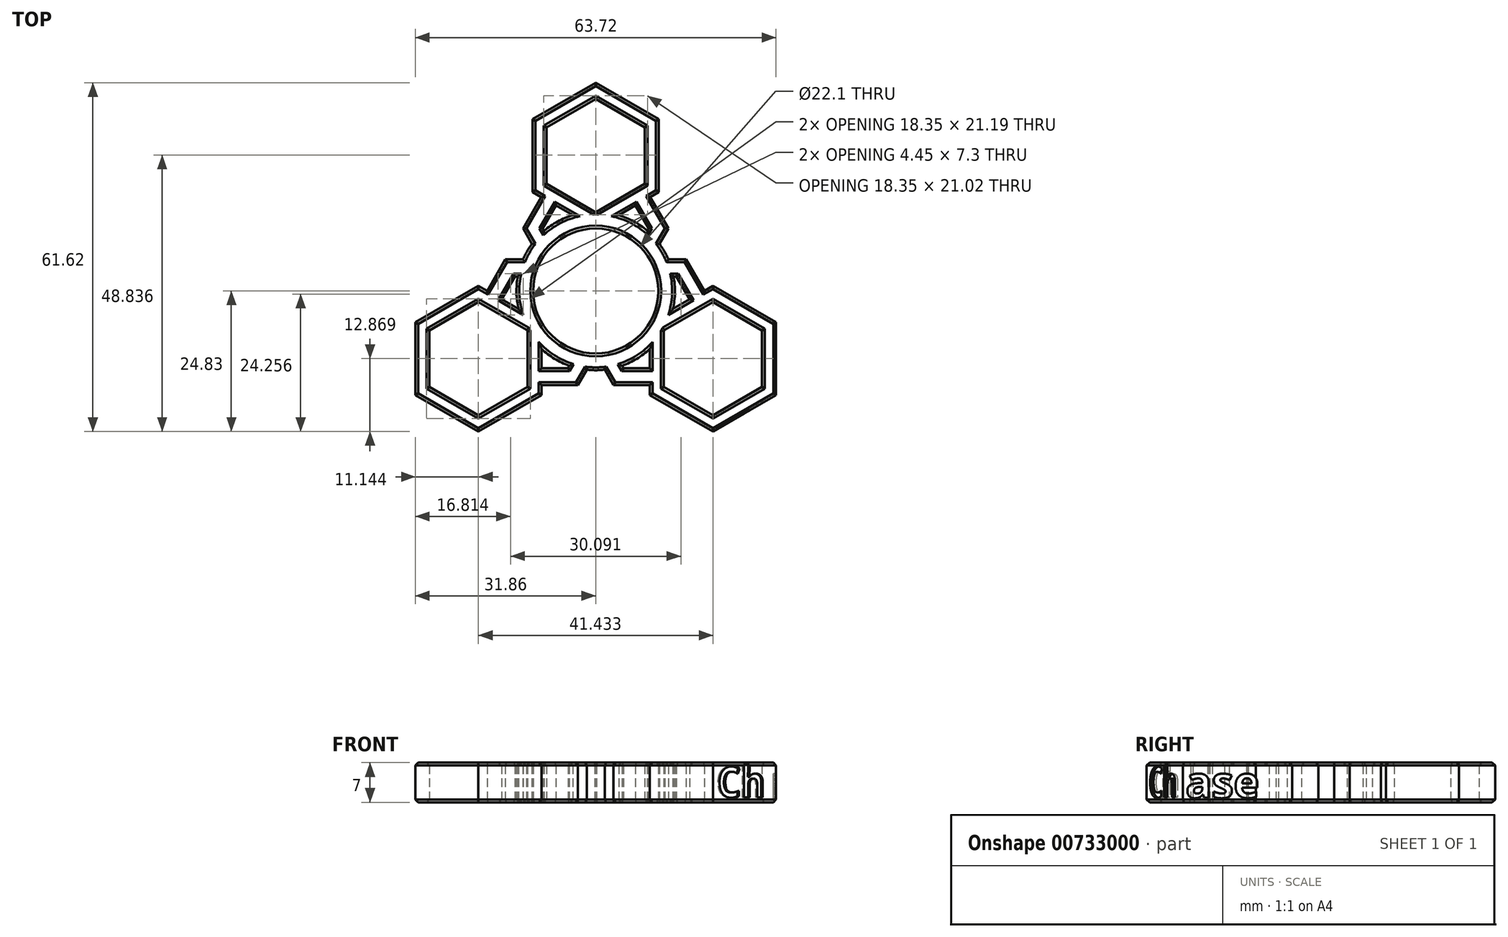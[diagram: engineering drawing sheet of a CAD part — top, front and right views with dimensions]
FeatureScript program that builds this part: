
annotation { "Feature Type Name" : "Feature", "Feature Type Description" : "" }
export const myFeature = defineFeature(function(context is Context, id is Id, definition is map)
    precondition{}
    {
        {
            var Q0;
            Q0=qCreatedBy(makeId("Top.planeOp"),FACE);
            var sketch = newSketch(context, id + "F0", { "sketchPlane" : qUnion([Q0])});
            skCircle(sketch, "E0", {"center": v(0, 0) * mm, "radius": 11.05 * mm});
            skCircle(sketch, "E1.cCircle", {"center": v(0, 23.92) * mm, "radius": 10.02 * mm, "construction": true});
            skLineSegment(sketch, "E1.0", {"start": v(0, 33.94) * mm, "end": v(8.68, 28.93) * mm});
            skLineSegment(sketch, "E1.1", {"start": v(8.67, 28.93) * mm, "end": v(8.68, 18.91) * mm});
            skLineSegment(sketch, "E1.2", {"start": v(8.67, 18.91) * mm, "end": v(0, 13.9) * mm});
            skLineSegment(sketch, "E1.3", {"start": v(0, 13.9) * mm, "end": v(-8.67, 18.91) * mm});
            skLineSegment(sketch, "E1.4", {"start": v(-8.67, 18.91) * mm, "end": v(-8.68, 28.93) * mm});
            skLineSegment(sketch, "E1.5", {"start": v(-8.67, 28.93) * mm, "end": v(0, 33.94) * mm});
            skCircle(sketch, "E2.cCircle", {"center": v(0, 11.05) * mm, "radius": 9.36 * mm, "construction": true});
            skLineSegment(sketch, "E2.0", {"start": v(9.36, 11.05) * mm, "end": v(4.68, 2.95) * mm});
            skLineSegment(sketch, "E2.1", {"start": v(4.68, 2.95) * mm, "end": v(-4.68, 2.95) * mm});
            skLineSegment(sketch, "E2.2", {"start": v(-4.68, 2.95) * mm, "end": v(-9.36, 11.05) * mm});
            skLineSegment(sketch, "E2.3", {"start": v(-9.36, 11.05) * mm, "end": v(-4.68, 19.15) * mm});
            skLineSegment(sketch, "E2.4", {"start": v(-4.68, 19.15) * mm, "end": v(4.68, 19.15) * mm});
            skLineSegment(sketch, "E2.5", {"start": v(4.68, 19.15) * mm, "end": v(9.36, 11.05) * mm});
            skLineSegment(sketch, "E3", {"start": v(0, 11.05) * mm, "end": v(30.07, 11.05) * mm, "construction": true});
            skLineSegment(sketch, "E4.0", {"start": v(-6.4, -0.05) * mm, "end": v(-12.82, 11.05) * mm});
            skLineSegment(sketch, "E4.1", {"start": v(-6.4, 22.15) * mm, "end": v(6.4, 22.15) * mm});
            skLineSegment(sketch, "E4.2", {"start": v(6.4, 22.15) * mm, "end": v(12.82, 11.05) * mm});
            skLineSegment(sketch, "E4.3", {"start": v(-12.82, 11.05) * mm, "end": v(-6.4, 22.15) * mm});
            skLineSegment(sketch, "E4.4", {"start": v(12.82, 11.05) * mm, "end": v(6.4, -0.05) * mm});
            skLineSegment(sketch, "E4.5", {"start": v(6.4, -0.05) * mm, "end": v(-6.4, -0.05) * mm});
            skCircle(sketch, "E5", {"center": v(0, 0) * mm, "radius": 14 * mm});
            skCircle(sketch, "E6.cCircle", {"center": v(0, 23.92) * mm, "radius": 12.87 * mm, "construction": true});
            skLineSegment(sketch, "E6.0", {"start": v(0, 11.05) * mm, "end": v(-11.15, 17.49) * mm});
            skLineSegment(sketch, "E6.1", {"start": v(-11.15, 17.49) * mm, "end": v(-11.15, 30.36) * mm});
            skLineSegment(sketch, "E6.2", {"start": v(-11.15, 30.36) * mm, "end": v(0, 36.8) * mm});
            skLineSegment(sketch, "E6.3", {"start": v(0, 36.8) * mm, "end": v(11.15, 30.36) * mm});
            skLineSegment(sketch, "E6.4", {"start": v(11.15, 30.36) * mm, "end": v(11.15, 17.49) * mm});
            skLineSegment(sketch, "E6.5", {"start": v(11.15, 17.49) * mm, "end": v(0, 11.05) * mm});
            skSolve(sketch);
        }
        {
            var Q0;
            {var subQ5=sQuery(id+"F0.wireOp",EDGE,"E1.0");Q0=makeQuery(id+"F0.imprint","IMPRINT",FACE,{"disambiguationData":[TD([[makeQuery(id+"F0.imprint","IMPRINT",EDGE,{"derivedFrom":subQ5}),1.0]])]});}
            var Q1;
            {var subQ1=sQuery(id+"F0.wireOp",EDGE,"E1.3");var subQ5=sQuery(id+"F0.wireOp",EDGE,"E1.4");var subQ6=makeQuery(id+"F0.imprint","INTERSECT",VERTEX,{"derivedFrom":[subQ1,subQ5]});Q1=makeQuery(id+"F0.imprint","IMPRINT",FACE,{"disambiguationData":[TD([[makeQuery(id+"F0.imprint","IMPRINT",EDGE,{"disambiguationData":[TD([[subQ6,1.0]])],"derivedFrom":subQ1}),1.0]])]});}
            var Q2;
            {var subQ1=sQuery(id+"F0.wireOp",EDGE,"E1.2");var subQ6=sQuery(id+"F0.wireOp",EDGE,"E1.3");var subQ13=makeQuery(id+"F0.imprint","INTERSECT",VERTEX,{"derivedFrom":[subQ1,subQ6]});Q2=makeQuery(id+"F0.imprint","IMPRINT",FACE,{"disambiguationData":[TD([[makeQuery(id+"F0.imprint","IMPRINT",EDGE,{"disambiguationData":[TD([[subQ13,1.0]])],"derivedFrom":subQ1}),1.0]])]});}
            var Q3;
            {var subQ3=sQuery(id+"F0.wireOp",EDGE,"E1.1");var subQ5=sQuery(id+"F0.wireOp",EDGE,"E1.2");var subQ6=makeQuery(id+"F0.imprint","INTERSECT",VERTEX,{"derivedFrom":[subQ3,subQ5]});Q3=makeQuery(id+"F0.imprint","IMPRINT",FACE,{"disambiguationData":[TD([[makeQuery(id+"F0.imprint","IMPRINT",EDGE,{"disambiguationData":[TD([[subQ6,1.0]])],"derivedFrom":subQ3}),1.0]])]});}
            var Q4;
            {var subQ5=sQuery(id+"F0.wireOp",EDGE,"E2.5");var subQ6=sQuery(id+"F0.wireOp",EDGE,"E2.0");var subQ7=makeQuery(id+"F0.imprint","INTERSECT",VERTEX,{"derivedFrom":[subQ6,subQ5]});Q4=makeQuery(id+"F0.imprint","IMPRINT",FACE,{"disambiguationData":[TD([[makeQuery(id+"F0.imprint","IMPRINT",EDGE,{"disambiguationData":[TD([[subQ7,-1.0]])],"derivedFrom":subQ6}),1.0]])]});}
            var Q5;
            {var subQ0=sQuery(id+"F0.wireOp",EDGE,"E2.0");var subQ1=sQuery(id+"F0.wireOp",EDGE,"E0");var subQ2=makeQuery(id+"F0.imprint","INTERSECT",VERTEX,{"derivedFrom":[subQ1,subQ0]});Q5=makeQuery(id+"F0.imprint","IMPRINT",FACE,{"disambiguationData":[TD([[makeQuery(id+"F0.imprint","IMPRINT",EDGE,{"disambiguationData":[TD([[subQ2,1.0]])],"derivedFrom":subQ1}),-1.0]])]});}
            var Q6;
            {var subQ1=sQuery(id+"F0.wireOp",EDGE,"E0");var subQ3=sQuery(id+"F0.wireOp",EDGE,"E2.0");var subQ4=makeQuery(id+"F0.imprint","INTERSECT",VERTEX,{"derivedFrom":[subQ1,subQ3]});Q6=makeQuery(id+"F0.imprint","IMPRINT",FACE,{"disambiguationData":[TD([[makeQuery(id+"F0.imprint","IMPRINT",EDGE,{"disambiguationData":[TD([[subQ4,1.0]])],"derivedFrom":subQ3}),-1.0]])]});}
            var Q7;
            {var subQ1=sQuery(id+"F0.wireOp",EDGE,"E0");var subQ3=sQuery(id+"F0.wireOp",EDGE,"E2.2");var subQ4=makeQuery(id+"F0.imprint","INTERSECT",VERTEX,{"derivedFrom":[subQ1,subQ3]});Q7=makeQuery(id+"F0.imprint","IMPRINT",FACE,{"disambiguationData":[TD([[makeQuery(id+"F0.imprint","IMPRINT",EDGE,{"disambiguationData":[TD([[subQ4,-1.0]])],"derivedFrom":subQ3}),-1.0]])]});}
            var Q8;
            {var subQ0=sQuery(id+"F0.wireOp",EDGE,"E6.5");var subQ1=sQuery(id+"F0.wireOp",EDGE,"E5");var subQ2=makeQuery(id+"F0.imprint","INTERSECT",VERTEX,{"derivedFrom":[subQ1,subQ0]});Q8=makeQuery(id+"F0.imprint","IMPRINT",FACE,{"disambiguationData":[TD([[makeQuery(id+"F0.imprint","IMPRINT",EDGE,{"disambiguationData":[TD([[subQ2,-1.0]])],"derivedFrom":subQ1}),1.0]])]});}
            var Q9;
            {var subQ0=sQuery(id+"F0.wireOp",EDGE,"E4.4");var subQ1=sQuery(id+"F0.wireOp",EDGE,"E0");var subQ2=makeQuery(id+"F0.imprint","INTERSECT",VERTEX,{"derivedFrom":[subQ1,subQ0]});Q9=makeQuery(id+"F0.imprint","IMPRINT",FACE,{"disambiguationData":[TD([[makeQuery(id+"F0.imprint","IMPRINT",EDGE,{"disambiguationData":[TD([[subQ2,1.0]])],"derivedFrom":subQ1}),-1.0]])]});}
            var Q10;
            {var subQ0=sQuery(id+"F0.wireOp",EDGE,"E2.2");var subQ1=sQuery(id+"F0.wireOp",EDGE,"E0");var subQ2=makeQuery(id+"F0.imprint","INTERSECT",VERTEX,{"derivedFrom":[subQ1,subQ0]});Q10=makeQuery(id+"F0.imprint","IMPRINT",FACE,{"disambiguationData":[TD([[makeQuery(id+"F0.imprint","IMPRINT",EDGE,{"disambiguationData":[TD([[subQ2,-1.0]])],"derivedFrom":subQ1}),-1.0]])]});}
            var Q11;
            {var subQ0=sQuery(id+"F0.wireOp",EDGE,"E2.3");var subQ1=sQuery(id+"F0.wireOp",EDGE,"E2.2");var subQ2=makeQuery(id+"F0.imprint","INTERSECT",VERTEX,{"derivedFrom":[subQ1,subQ0]});Q11=makeQuery(id+"F0.imprint","IMPRINT",FACE,{"disambiguationData":[TD([[makeQuery(id+"F0.imprint","IMPRINT",EDGE,{"disambiguationData":[TD([[subQ2,1.0]])],"derivedFrom":subQ1}),1.0]])]});}
            var Q12;
            {var subQ0=sQuery(id+"F0.wireOp",EDGE,"E5");var subQ1=sQuery(id+"F0.wireOp",EDGE,"E1.3");var subQ2=makeQuery(id+"F0.imprint","INTERSECT",VERTEX,{"derivedFrom":[subQ1,subQ0]});Q12=makeQuery(id+"F0.imprint","IMPRINT",FACE,{"disambiguationData":[TD([[makeQuery(id+"F0.imprint","IMPRINT",EDGE,{"disambiguationData":[TD([[subQ2,-1.0]])],"derivedFrom":subQ1}),1.0]])]});}
            var Q13;
            {var subQ0=sQuery(id+"F0.wireOp",EDGE,"E2.3");var subQ1=sQuery(id+"F0.wireOp",EDGE,"E1.3");var subQ2=makeQuery(id+"F0.imprint","INTERSECT",VERTEX,{"derivedFrom":[subQ1,subQ0]});Q13=makeQuery(id+"F0.imprint","IMPRINT",FACE,{"disambiguationData":[TD([[makeQuery(id+"F0.imprint","IMPRINT",EDGE,{"disambiguationData":[TD([[subQ2,-1.0]])],"derivedFrom":subQ1}),1.0]])]});}
            var Q14;
            {var subQ0=sQuery(id+"F0.wireOp",EDGE,"E4.2");var subQ1=sQuery(id+"F0.wireOp",EDGE,"E1.2");var subQ2=makeQuery(id+"F0.imprint","INTERSECT",VERTEX,{"derivedFrom":[subQ1,subQ0]});Q14=makeQuery(id+"F0.imprint","IMPRINT",FACE,{"disambiguationData":[TD([[makeQuery(id+"F0.imprint","IMPRINT",EDGE,{"disambiguationData":[TD([[subQ2,-1.0]])],"derivedFrom":subQ1}),1.0]])]});}
            var Q15;
            {var subQ0=sQuery(id+"F0.wireOp",EDGE,"E2.5");var subQ1=sQuery(id+"F0.wireOp",EDGE,"E1.2");var subQ2=makeQuery(id+"F0.imprint","INTERSECT",VERTEX,{"derivedFrom":[subQ1,subQ0]});Q15=makeQuery(id+"F0.imprint","IMPRINT",FACE,{"disambiguationData":[TD([[makeQuery(id+"F0.imprint","IMPRINT",EDGE,{"disambiguationData":[TD([[subQ2,-1.0]])],"derivedFrom":subQ1}),1.0]])]});}
            extrude(context, id + "F1", {"entities" : qUnion([Q0, Q1, Q2, Q3, Q4, Q5, Q6, Q7, Q8, Q9, Q10, Q11, Q12, Q13, Q14, Q15]), "depth" : 7 * mm, "offsetDistance" : 25 * mm});
        }
        {
            var Q0;
            Q0=qCreatedBy(makeId("Right.planeOp"),FACE);
            var sketch = newSketch(context, id + "F2", { "sketchPlane" : qUnion([Q0])});
            skLineSegment(sketch, "E7", {"start": v(0, 0) * mm, "end": v(0, 30.07) * mm});
            skSolve(sketch);
        }
        {
            var Q0;
            Q0=makeQuery(id+"F1.opExtrude","SWEPT_BODY",BODY,{"disambiguationData":[OSD([sQuery(id+"F0.wireOp",EDGE,"E0"),sQuery(id+"F0.wireOp",EDGE,"E1.0"),sQuery(id+"F0.wireOp",EDGE,"E1.1"),sQuery(id+"F0.wireOp",EDGE,"E1.2"),sQuery(id+"F0.wireOp",EDGE,"E1.3"),sQuery(id+"F0.wireOp",EDGE,"E1.4"),sQuery(id+"F0.wireOp",EDGE,"E1.5"),sQuery(id+"F0.wireOp",EDGE,"E2.0"),sQuery(id+"F0.wireOp",EDGE,"E2.2"),sQuery(id+"F0.wireOp",EDGE,"E2.3"),sQuery(id+"F0.wireOp",EDGE,"E2.5"),sQuery(id+"F0.wireOp",EDGE,"E4.0"),sQuery(id+"F0.wireOp",EDGE,"E4.2"),sQuery(id+"F0.wireOp",EDGE,"E4.3"),sQuery(id+"F0.wireOp",EDGE,"E4.4"),sQuery(id+"F0.wireOp",EDGE,"E5"),sQuery(id+"F0.wireOp",EDGE,"E6.0"),sQuery(id+"F0.wireOp",EDGE,"E6.1"),sQuery(id+"F0.wireOp",EDGE,"E6.2"),sQuery(id+"F0.wireOp",EDGE,"E6.3"),sQuery(id+"F0.wireOp",EDGE,"E6.4"),sQuery(id+"F0.wireOp",EDGE,"E6.5")])]});
            var Q1;
            Q1=sQuery(id+"F2.wireOp",EDGE,"E7");
            circularPattern(context, id + "F3", {"operationType" : NewBodyOperationType.ADD, "entities" : qUnion([Q0]), "axis" : qUnion([Q1]), "angle" : 360 * degree, "instanceCount" : 3, "equalSpace" : true});
        }
        {
            var Q0;
            Q0=makeQuery(id+"F3.opPattern","COPY",FACE,{"derivedFrom":makeQuery(id+"F1.opExtrude","SWEPT_FACE",FACE,{"disambiguationData":[OSD([sQuery(id+"F0.wireOp",EDGE,"E6.3")])]}),"instanceName":"2"});
            var sketch = newSketch(context, id + "F4", { "sketchPlane" : qUnion([Q0])});
            skText(sketch, "E8", { "text": "Ch", "fontName": "OpenSans-Bold.ttf"});
            const initialGuessF4  = {"E8": [0.00642, 0.00086, 1, 0, 0.00546]};
            skSetInitialGuess(sketch, initialGuessF4);
            skSolve(sketch);
        }
        {
            var Q0;
            Q0=makeQuery(id+"F3.opPattern","COPY",FACE,{"derivedFrom":makeQuery(id+"F1.opExtrude","SWEPT_FACE",FACE,{"disambiguationData":[OSD([sQuery(id+"F0.wireOp",EDGE,"E6.2")])]}),"instanceName":"2"});
            var sketch = newSketch(context, id + "F5", { "sketchPlane" : qUnion([Q0])});
            skText(sketch, "E9", { "text": "ase", "fontName": "OpenSans-Bold.ttf"});
            const initialGuessF5  = {"E9": [-0.01792, 0.00078, 1, 0, 0.00555]};
            skSetInitialGuess(sketch, initialGuessF5);
            skSolve(sketch);
        }
        {
            var Q0;
            Q0 = qSketchRegion(id + "F4", true);
            extrude(context, id + "F6", {"entities" : qUnion([Q0]), "operationType" : NewBodyOperationType.REMOVE, "oppositeDirection" : true, "depth" : .5 * mm, "offsetDistance" : 25 * mm});
        }
        {
            var Q0;
            Q0 = qSketchRegion(id + "F5", true);
            extrude(context, id + "F7", {"entities" : qUnion([Q0]), "operationType" : NewBodyOperationType.REMOVE, "oppositeDirection" : true, "depth" : .5 * mm, "offsetDistance" : 25 * mm});
        }
        {
            var Q0;
            Q0=makeQuery(id+"F3.opPattern","COPY",EDGE,{"derivedFrom":makeQuery(id+"F1.opExtrude","CAP_EDGE",EDGE,{"disambiguationData":[OSD([sQuery(id+"F0.wireOp",EDGE,"E6.1")])],"isStart":false}),"instanceName":"2"});
            var Q1;
            Q1=makeQuery(id+"F3.opPattern","COPY",EDGE,{"derivedFrom":makeQuery(id+"F1.opExtrude","CAP_EDGE",EDGE,{"disambiguationData":[OSD([sQuery(id+"F0.wireOp",EDGE,"E6.2")])],"isStart":false}),"instanceName":"2"});
            var Q2;
            Q2=makeQuery(id+"F3.opPattern","COPY",EDGE,{"derivedFrom":makeQuery(id+"F1.opExtrude","CAP_EDGE",EDGE,{"disambiguationData":[OSD([sQuery(id+"F0.wireOp",EDGE,"E6.3")])],"isStart":false}),"instanceName":"2"});
            var Q3;
            Q3=makeQuery(id+"F3.opPattern","COPY",EDGE,{"derivedFrom":makeQuery(id+"F1.opExtrude","CAP_EDGE",EDGE,{"disambiguationData":[OSD([sQuery(id+"F0.wireOp",EDGE,"E6.4")])],"isStart":false}),"instanceName":"2"});
            var Q4;
            {var subQ0=sQuery(id+"F0.wireOp",EDGE,"E6.5");Q4=makeQuery(id+"F3.opPattern","COPY",EDGE,{"derivedFrom":makeQuery(id+"F1.opExtrude","CAP_EDGE",EDGE,{"disambiguationData":[OSD([subQ0]),TDD([makeQuery(id+"F0.imprint","IMPRINT",EDGE,{"disambiguationData":[TD([[makeQuery(id+"F0.imprint","INTERSECT",VERTEX,{"derivedFrom":[sQuery(id+"F0.wireOp",EDGE,"E6.4"),subQ0]}),-1.0]])],"derivedFrom":subQ0})])],"isStart":false}),"instanceName":"2"});}
            var Q5;
            Q5=makeQuery(id+"F3.opPattern","COPY",EDGE,{"derivedFrom":makeQuery(id+"F1.opExtrude","CAP_EDGE",EDGE,{"disambiguationData":[OSD([sQuery(id+"F0.wireOp",EDGE,"E4.2")])],"isStart":false}),"instanceName":"2"});
            var Q6;
            Q6=makeQuery(id+"F3.opPattern","COPY",EDGE,{"derivedFrom":makeQuery(id+"F1.opExtrude","CAP_EDGE",EDGE,{"disambiguationData":[OSD([sQuery(id+"F0.wireOp",EDGE,"E4.4")])],"isStart":false}),"instanceName":"2"});
            var Q7;
            {var subQ0=sQuery(id+"F0.wireOp",EDGE,"E4.0");var subQ1=sQuery(id+"F0.wireOp",EDGE,"E5");var subQ4=makeQuery(id+"F0.imprint","IMPRINT",EDGE,{"disambiguationData":[TD([[makeQuery(id+"F0.imprint","INTERSECT",VERTEX,{"derivedFrom":[subQ0,subQ1]}),-1.0]])],"derivedFrom":subQ1});Q7=makeQuery(id+"F3.boolean.opBoolean","SPLIT",EDGE,{"disambiguationData":[TD([makeQuery(id+"F3.opPattern","COPY",FACE,{"derivedFrom":makeQuery(id+"F1.opExtrude","SWEPT_FACE",FACE,{"disambiguationData":[OSD([subQ0])]}),"instanceName":"1"})])],"derivedFrom":makeQuery(id+"F1.opExtrude","CAP_EDGE",EDGE,{"disambiguationData":[OSD([subQ1]),TDD([subQ4])],"isStart":false})});}
            var Q8;
            Q8=makeQuery(id+"F3.opPattern","COPY",EDGE,{"derivedFrom":makeQuery(id+"F1.opExtrude","CAP_EDGE",EDGE,{"disambiguationData":[OSD([sQuery(id+"F0.wireOp",EDGE,"E4.0")])],"isStart":false}),"instanceName":"1"});
            var Q9;
            Q9=makeQuery(id+"F3.opPattern","COPY",EDGE,{"derivedFrom":makeQuery(id+"F1.opExtrude","CAP_EDGE",EDGE,{"disambiguationData":[OSD([sQuery(id+"F0.wireOp",EDGE,"E4.3")])],"isStart":false}),"instanceName":"1"});
            var Q10;
            {var subQ0=makeQuery(id+"F1.opExtrude","CAP_FACE",FACE,{"disambiguationData":[OSD([sQuery(id+"F0.wireOp",EDGE,"E0"),sQuery(id+"F0.wireOp",EDGE,"E1.0"),sQuery(id+"F0.wireOp",EDGE,"E1.1"),sQuery(id+"F0.wireOp",EDGE,"E1.2"),sQuery(id+"F0.wireOp",EDGE,"E1.3"),sQuery(id+"F0.wireOp",EDGE,"E1.4"),sQuery(id+"F0.wireOp",EDGE,"E1.5"),sQuery(id+"F0.wireOp",EDGE,"E2.0"),sQuery(id+"F0.wireOp",EDGE,"E2.2"),sQuery(id+"F0.wireOp",EDGE,"E2.3"),sQuery(id+"F0.wireOp",EDGE,"E2.5"),sQuery(id+"F0.wireOp",EDGE,"E4.0"),sQuery(id+"F0.wireOp",EDGE,"E4.2"),sQuery(id+"F0.wireOp",EDGE,"E4.3"),sQuery(id+"F0.wireOp",EDGE,"E4.4"),sQuery(id+"F0.wireOp",EDGE,"E5"),sQuery(id+"F0.wireOp",EDGE,"E6.0"),sQuery(id+"F0.wireOp",EDGE,"E6.1"),sQuery(id+"F0.wireOp",EDGE,"E6.2"),sQuery(id+"F0.wireOp",EDGE,"E6.3"),sQuery(id+"F0.wireOp",EDGE,"E6.4"),sQuery(id+"F0.wireOp",EDGE,"E6.5")])],"isStart":false});Q10=makeQuery(id+"F3.boolean.opBoolean","MERGE",FACE,{"derivedFrom":[subQ0,makeQuery(id+"F3.opPattern","COPY",FACE,{"derivedFrom":subQ0,"instanceName":"1"}),makeQuery(id+"F3.opPattern","COPY",FACE,{"derivedFrom":subQ0,"instanceName":"2"})]});}
            var Q11;
            {var subQ0=makeQuery(id+"F1.opExtrude","CAP_FACE",FACE,{"disambiguationData":[OSD([sQuery(id+"F0.wireOp",EDGE,"E0"),sQuery(id+"F0.wireOp",EDGE,"E1.0"),sQuery(id+"F0.wireOp",EDGE,"E1.1"),sQuery(id+"F0.wireOp",EDGE,"E1.2"),sQuery(id+"F0.wireOp",EDGE,"E1.3"),sQuery(id+"F0.wireOp",EDGE,"E1.4"),sQuery(id+"F0.wireOp",EDGE,"E1.5"),sQuery(id+"F0.wireOp",EDGE,"E2.0"),sQuery(id+"F0.wireOp",EDGE,"E2.2"),sQuery(id+"F0.wireOp",EDGE,"E2.3"),sQuery(id+"F0.wireOp",EDGE,"E2.5"),sQuery(id+"F0.wireOp",EDGE,"E4.0"),sQuery(id+"F0.wireOp",EDGE,"E4.2"),sQuery(id+"F0.wireOp",EDGE,"E4.3"),sQuery(id+"F0.wireOp",EDGE,"E4.4"),sQuery(id+"F0.wireOp",EDGE,"E5"),sQuery(id+"F0.wireOp",EDGE,"E6.0"),sQuery(id+"F0.wireOp",EDGE,"E6.1"),sQuery(id+"F0.wireOp",EDGE,"E6.2"),sQuery(id+"F0.wireOp",EDGE,"E6.3"),sQuery(id+"F0.wireOp",EDGE,"E6.4"),sQuery(id+"F0.wireOp",EDGE,"E6.5")])],"isStart":true});Q11=makeQuery(id+"F3.boolean.opBoolean","MERGE",FACE,{"derivedFrom":[subQ0,makeQuery(id+"F3.opPattern","COPY",FACE,{"derivedFrom":subQ0,"instanceName":"1"}),makeQuery(id+"F3.opPattern","COPY",FACE,{"derivedFrom":subQ0,"instanceName":"2"})]});}
            chamfer(context, id + "F8", {"entities" : qUnion([Q0, Q1, Q2, Q3, Q4, Q5, Q6, Q7, Q8, Q9, Q10, Q11]), "width" : .5 * mm, "tangentPropagation" : true});
        }
    });
